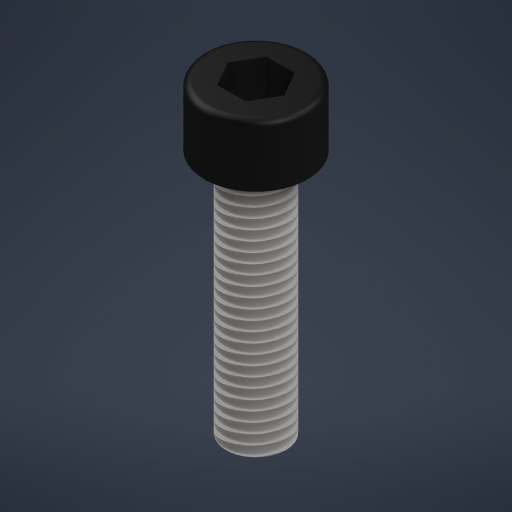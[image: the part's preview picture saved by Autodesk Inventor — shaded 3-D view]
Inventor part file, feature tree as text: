
AUTODESK INVENTOR PART (.ipt)
format: ipt  version: 2024 (Build 280153000, 153)  size: 250,368 bytes
history: native  units: mm
features: extrude x3, sketch x1, fillet x1, thread x1
ambient origin geometry x8: Origin, YZ Plane, XZ Plane, XY Plane, X Axis, Y Axis, Z Axis, Center Point
bodies: Solid1 (feature_tree)
feature tree (6):
  sketch  "Sketch1"  dims[d0=4.88mm d1=8.4mm d2=5.0mm d3=0.0mm d4=20.0mm d5=0.0mm d8=4.0mm d9=3.0mm d10=0.0mm d11=0.5mm d12=20.0mm d13=0.0mm]
  extrude  "Extrusion1"  Depth=20.0mm
  extrude  "Extrusion2"  Depth=5.0mm TaperAngle=0.0deg
  extrude  "Extrusion3"  Depth=20.0mm
  fillet  "Fillet1"  [1 undecoded]
  thread  "Thread2"  [1 undecoded]
note: 2 required parameter values undecoded (feature->parameter linkage not recoverable at this tier; creation-order binding heuristic only, values carry confidence <= 0.55)
